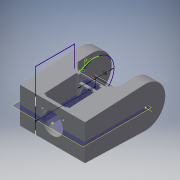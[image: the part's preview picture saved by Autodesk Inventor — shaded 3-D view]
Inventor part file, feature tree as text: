
AUTODESK INVENTOR PART (.ipt)
format: ipt  version: 2018 (Build 220112000, 112)  size: 537,600 bytes
history: native  units: mm
features: sketch x27, projected_geometry x25, extrude x22, other x8, hole x3, fillet x3, chamfer x2, mirror x1, plane x1, reference x1
ambient origin geometry x8: Origin, YZ Plane, XZ Plane, XY Plane, X Axis, Y Axis, Z Axis, Center Point
bodies: Solid1 (feature_tree)
feature tree (93):
  extrude  "Extrusion1"  Depth=45.0mm
  extrude  "Extrusion2"  Depth=1.95mm
  hole  "Hole1"  [1 undecoded]
  hole  "Hole2"  [1 undecoded]
  fillet  "Fillet1"  Radius=14.0mm
  extrude  "Extrusion3"  Depth=18.5mm
  extrude  "Extrusion4"  Depth=10.0mm
  extrude  "Extrusion5"  Depth=2.195mm
  extrude  "Extrusion6"  Depth=20.5mm
  hole  "Hole3"  [1 undecoded]
  extrude  "Extrusion7"  Depth=0.5mm
  extrude  "Extrusion8"  Depth=1.0mm TaperAngle=0.0deg
  extrude  "Extrusion9"  Depth=24.5mm
  extrude  "Extrusion10"  Depth=10.0mm
  extrude  "Extrusion11"  Depth=14.5mm
  extrude  "Extrusion13"  Depth=14.5mm
  extrude  "Extrusion14"  Depth=5.0mm
  extrude  "Extrusion15"  Depth=2.25mm
  extrude  "Extrusion16"  Depth=5.0mm
  extrude  "Extrusion17"  Depth=9.0mm
  chamfer  "Chamfer1"  Distance=1.0mm
  fillet  "Fillet7"  Radius=20.7mm
  fillet  "Fillet8"  Radius=32.0mm
  mirror  "Mirror1"
  sketch  "Sketch26"  dims[d55=2.25mm d56=5.0mm]
  extrude  "Extrusion24"  Depth=3.0mm TaperAngle=0.0deg
  extrude  "Extrusion25"  Depth=8.0mm
  extrude  "Extrusion26"  Depth=41.5mm TaperAngle=0.0deg
  extrude  "Extrusion27"  Depth=41.5mm TaperAngle=0.0deg
  other  "Work Axis1"
  plane  "Work Plane2"
  extrude  "Extrusion28"  Depth=41.5mm TaperAngle=0.0deg
  extrude  "Extrusion29"  Depth=41.5mm TaperAngle=0.0deg
  chamfer  "Chamfer2"  Distance=0.2mm
  sketch  "Sketch38"  dims[d81=4.5mm d82=0.0mm d84=0.2mm d85=0.0mm d91=8.0mm d92=0.0mm d93=5.0mm d94=0.0mm d95=5.0mm d96=0.0mm d98=0.2mm d99=0.0mm d100=0.2mm d101=0.0mm d102=2.5mm d103=2.0mm d104=45.0deg d105=1.5mm d114=0.5mm d130=60.0mm d131=36.0mm d146=40.0mm d147=58.0mm d148=0.0mm d149=2.0mm d150=15.0mm d151=0.0mm d152=15.0mm d153=0.0mm d154=15.0mm d155=0.0mm d156=15.0mm d157=0.0mm d158=20.5mm d159=41.5mm d160=14.0mm d161=14.0mm d162=7.0mm d165=100.0mm d166=0.0mm d167=100.0mm d168=0.0mm d169=6.0mm d170=2.0mm d171=45.0deg]
  sketch  "Sketch1"  dims[d0=24.5mm d1=45.0mm]
  sketch  "Sketch2"  dims[d2=1.95mm d3=0.0mm d4=2.25mm]
  projected_geometry  "Projected Loop1"
  sketch  "Sketch3"  dims[d5=20.0mm d6=2.25mm]
  projected_geometry  "Projected Loop2"
  sketch  "Sketch4"  dims[d7=5.25mm d8=5.25mm d9=14.0mm]
  projected_geometry  "Projected Loop3"
  sketch  "Sketch5"  dims[d10=5.25mm d11=18.5mm]
  projected_geometry  "Projected Loop4"
  sketch  "Sketch6"  dims[d12=10.0mm d13=0.0mm d14=20.5mm]
  projected_geometry  "Projected Loop5"
  sketch  "Sketch7"  dims[d15=2.0mm d16=2.195mm]
  projected_geometry  "Projected Loop6"
  sketch  "Sketch8"  dims[d17=2.0mm]
  projected_geometry  "Projected Loop7"
  sketch  "Sketch9"  dims[d18=2.4mm d19=6.0mm d20=4.4mm d21=2.0mm d22=90.0deg d23=8.0mm d24=20.594885mm d25=20.5mm]
  projected_geometry  "Projected Loop8"
  projected_geometry  "Projected Loop9"
  sketch  "Sketch10"  dims[d26=26.65mm d27=2.0mm]
  projected_geometry  "Projected Loop10"
  projected_geometry  "Projected Loop11"
  sketch  "Sketch11"  dims[d28=2.0mm]
  projected_geometry  "Projected Loop12"
  sketch  "Sketch12"  dims[d29=2.4mm d30=6.0mm d31=4.4mm d32=2.0mm d33=90.0deg d34=8.0mm d35=20.594885mm d36=0.5mm]
  sketch  "Sketch13"  dims[d37=18.0mm d38=1.0mm d39=0.0mm]
  sketch  "Sketch14"  dims[d41=5.0mm d42=0.0mm d43=24.5mm]
  projected_geometry  "Projected Loop13"
  sketch  "Sketch16"  dims[d44=1.15mm d45=0.0mm d46=10.0mm]
  projected_geometry  "Projected Loop14"
  sketch  "Sketch17"  dims[d47=21.0mm d48=14.5mm]
  projected_geometry  "Projected Loop15"
  sketch  "Sketch18"  dims[d49=20.0mm d50=14.5mm]
  projected_geometry  "Projected Loop16"
  sketch  "Sketch19"  dims[d51=24.5mm d52=5.0mm]
  projected_geometry  "Projected Loop17"
  sketch  "Sketch20"  dims[d53=5.0mm d54=2.25mm]
  projected_geometry  "Projected Loop18"
  projected_geometry  "Projected Loop25"
  sketch  "Sketch31"  dims[d57=5.0mm d58=9.0mm]
  projected_geometry  "Projected Loop30"
  reference  "Reference1"
  sketch  "Sketch32"  dims[d59=14.75mm]
  projected_geometry  "Projected Loop31"
  sketch  "Sketch33"  dims[d60=4.0mm d61=1.0mm d62=0.0mm d63=20.7mm]
  projected_geometry  "Projected Loop32"
  sketch  "Sketch34"  dims[d64=2.4mm d65=6.0mm d66=4.4mm d67=2.0mm d68=90.0deg d69=8.0mm d70=20.594885mm d72=32.0mm]
  projected_geometry  "Projected Loop33"
  other  "Work Point1"
  other  "Work Point2"
  other  "Work Point3"
  sketch  "Sketch35"  dims[d73=3.0mm d74=0.0mm d75=1.0mm d76=0.0mm]
  sketch  "Sketch37"  dims[d77=12.25mm d78=0.0mm d80=8.0mm]
  projected_geometry  "Projected Loop34"
  parser-record x1  (decoder bookkeeping rows leaked as tree rows — omitted from the tree; the rows remain in map.json)
  other  "servocheck.iam"
  other  "LX-16A:3"
  other  "DUOPAN-SG-SJ_10"
  projected_geometry  "Project Cut Edges1"
note: 3 required parameter values undecoded (feature->parameter linkage not recoverable at this tier; creation-order binding heuristic only, values carry confidence <= 0.55)
note: 1 file-system path scrubbed to <path> (originals preserved in map.json)
